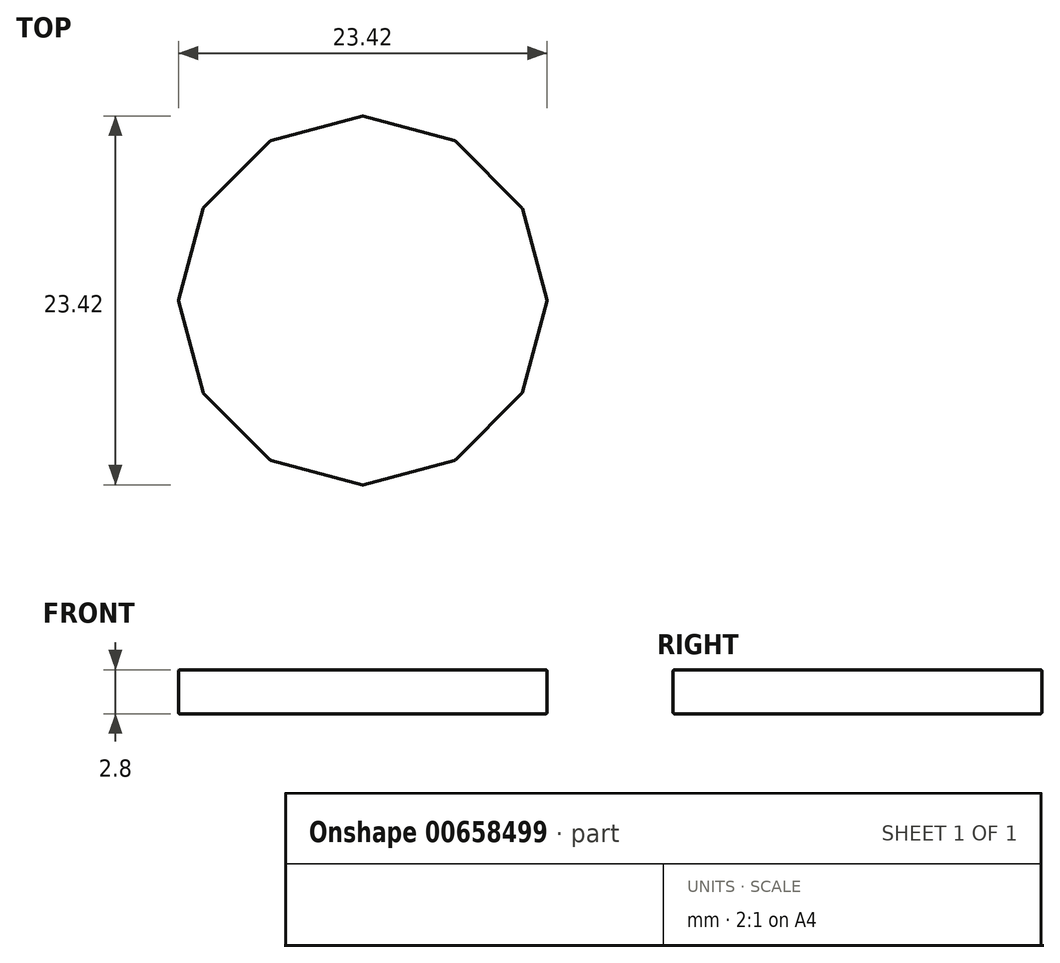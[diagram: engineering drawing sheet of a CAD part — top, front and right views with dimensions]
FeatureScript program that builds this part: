
annotation { "Feature Type Name" : "Feature", "Feature Type Description" : "" }
export const myFeature = defineFeature(function(context is Context, id is Id, definition is map)
    precondition{}
    {
        {
            var Q0;
            Q0=qCreatedBy(makeId("Top.planeOp"),FACE);
            var sketch = newSketch(context, id + "F0", { "sketchPlane" : qUnion([Q0])});
            skCircle(sketch, "E0.cCircle", {"center": v(0, 0) * mm, "radius": 11.71 * mm, "construction": true});
            skLineSegment(sketch, "E0.0", {"start": v(5.86, 10.15) * mm, "end": v(10.15, 5.86) * mm});
            skLineSegment(sketch, "E0.1", {"start": v(10.15, 5.86) * mm, "end": v(11.72, 0) * mm});
            skLineSegment(sketch, "E0.2", {"start": v(11.72, 0) * mm, "end": v(10.15, -5.86) * mm});
            skLineSegment(sketch, "E0.3", {"start": v(10.15, -5.86) * mm, "end": v(5.86, -10.15) * mm});
            skLineSegment(sketch, "E0.4", {"start": v(5.86, -10.15) * mm, "end": v(0, -11.72) * mm});
            skLineSegment(sketch, "E0.5", {"start": v(0, -11.72) * mm, "end": v(-5.86, -10.15) * mm});
            skLineSegment(sketch, "E0.6", {"start": v(-5.86, -10.15) * mm, "end": v(-10.15, -5.86) * mm});
            skLineSegment(sketch, "E0.7", {"start": v(-10.15, -5.86) * mm, "end": v(-11.72, 0) * mm});
            skLineSegment(sketch, "E0.8", {"start": v(-11.72, 0) * mm, "end": v(-10.15, 5.86) * mm});
            skLineSegment(sketch, "E0.9", {"start": v(-10.15, 5.86) * mm, "end": v(-5.86, 10.15) * mm});
            skLineSegment(sketch, "E0.10", {"start": v(-5.86, 10.15) * mm, "end": v(0, 11.72) * mm});
            skLineSegment(sketch, "E0.11", {"start": v(0, 11.72) * mm, "end": v(5.86, 10.15) * mm});
            skSolve(sketch);
        }
        {
            var Q0;
            Q0 = qSketchRegion(id + "F0", true);
            extrude(context, id + "F1", {"entities" : qUnion([Q0]), "depth" : 2.8 * mm, "offsetDistance" : 25 * mm});
        }
        {
            var Q0;
            Q0=makeQuery(id+"F1.opExtrude","CAP_FACE",FACE,{"disambiguationData":[OSD([sQuery(id+"F0.wireOp",EDGE,"E0.0"),sQuery(id+"F0.wireOp",EDGE,"E0.1"),sQuery(id+"F0.wireOp",EDGE,"E0.2"),sQuery(id+"F0.wireOp",EDGE,"E0.3"),sQuery(id+"F0.wireOp",EDGE,"E0.4"),sQuery(id+"F0.wireOp",EDGE,"E0.5"),sQuery(id+"F0.wireOp",EDGE,"E0.6"),sQuery(id+"F0.wireOp",EDGE,"E0.7"),sQuery(id+"F0.wireOp",EDGE,"E0.8"),sQuery(id+"F0.wireOp",EDGE,"E0.9"),sQuery(id+"F0.wireOp",EDGE,"E0.10"),sQuery(id+"F0.wireOp",EDGE,"E0.11")])],"isStart":false});
            var Q1;
            Q1=makeQuery(id+"F1.opExtrude","CAP_FACE",FACE,{"disambiguationData":[OSD([sQuery(id+"F0.wireOp",EDGE,"E0.0"),sQuery(id+"F0.wireOp",EDGE,"E0.1"),sQuery(id+"F0.wireOp",EDGE,"E0.2"),sQuery(id+"F0.wireOp",EDGE,"E0.3"),sQuery(id+"F0.wireOp",EDGE,"E0.4"),sQuery(id+"F0.wireOp",EDGE,"E0.5"),sQuery(id+"F0.wireOp",EDGE,"E0.6"),sQuery(id+"F0.wireOp",EDGE,"E0.7"),sQuery(id+"F0.wireOp",EDGE,"E0.8"),sQuery(id+"F0.wireOp",EDGE,"E0.9"),sQuery(id+"F0.wireOp",EDGE,"E0.10"),sQuery(id+"F0.wireOp",EDGE,"E0.11")])],"isStart":true});
            var Q2;
            Q2=makeQuery(id+"F1.opExtrude","SWEPT_EDGE",EDGE,{"disambiguationData":[OSD([sQuery(id+"F0.wireOp",EDGE,"E0.8"),sQuery(id+"F0.wireOp",EDGE,"E0.9")])]});
            var Q3;
            Q3=makeQuery(id+"F1.opExtrude","SWEPT_EDGE",EDGE,{"disambiguationData":[OSD([sQuery(id+"F0.wireOp",EDGE,"E0.7"),sQuery(id+"F0.wireOp",EDGE,"E0.8")])]});
            var Q4;
            Q4=makeQuery(id+"F1.opExtrude","SWEPT_EDGE",EDGE,{"disambiguationData":[OSD([sQuery(id+"F0.wireOp",EDGE,"E0.6"),sQuery(id+"F0.wireOp",EDGE,"E0.7")])]});
            var Q5;
            Q5=makeQuery(id+"F1.opExtrude","SWEPT_EDGE",EDGE,{"disambiguationData":[OSD([sQuery(id+"F0.wireOp",EDGE,"E0.5"),sQuery(id+"F0.wireOp",EDGE,"E0.6")])]});
            var Q6;
            Q6=makeQuery(id+"F1.opExtrude","SWEPT_EDGE",EDGE,{"disambiguationData":[OSD([sQuery(id+"F0.wireOp",EDGE,"E0.4"),sQuery(id+"F0.wireOp",EDGE,"E0.5")])]});
            var Q7;
            Q7=makeQuery(id+"F1.opExtrude","SWEPT_EDGE",EDGE,{"disambiguationData":[OSD([sQuery(id+"F0.wireOp",EDGE,"E0.3"),sQuery(id+"F0.wireOp",EDGE,"E0.4")])]});
            var Q8;
            Q8=makeQuery(id+"F1.opExtrude","SWEPT_EDGE",EDGE,{"disambiguationData":[OSD([sQuery(id+"F0.wireOp",EDGE,"E0.2"),sQuery(id+"F0.wireOp",EDGE,"E0.3")])]});
            var Q9;
            Q9=makeQuery(id+"F1.opExtrude","SWEPT_EDGE",EDGE,{"disambiguationData":[OSD([sQuery(id+"F0.wireOp",EDGE,"E0.1"),sQuery(id+"F0.wireOp",EDGE,"E0.2")])]});
            var Q10;
            Q10=makeQuery(id+"F1.opExtrude","SWEPT_EDGE",EDGE,{"disambiguationData":[OSD([sQuery(id+"F0.wireOp",EDGE,"E0.0"),sQuery(id+"F0.wireOp",EDGE,"E0.1")])]});
            var Q11;
            Q11=makeQuery(id+"F1.opExtrude","SWEPT_EDGE",EDGE,{"disambiguationData":[OSD([sQuery(id+"F0.wireOp",EDGE,"E0.0"),sQuery(id+"F0.wireOp",EDGE,"E0.11")])]});
            var Q12;
            Q12=makeQuery(id+"F1.opExtrude","SWEPT_EDGE",EDGE,{"disambiguationData":[OSD([sQuery(id+"F0.wireOp",EDGE,"E0.10"),sQuery(id+"F0.wireOp",EDGE,"E0.11")])]});
            var Q13;
            Q13=makeQuery(id+"F1.opExtrude","SWEPT_EDGE",EDGE,{"disambiguationData":[OSD([sQuery(id+"F0.wireOp",EDGE,"E0.9"),sQuery(id+"F0.wireOp",EDGE,"E0.10")])]});
            fillet(context, id + "F2", {"entities" : qUnion([Q0, Q1, Q2, Q3, Q4, Q5, Q6, Q7, Q8, Q9, Q10, Q11, Q12, Q13]), "tangentPropagation" : true, "radius" : 0.1 * mm, "defaultsChanged" : true, "vertexSettings" : [], "allowEdgeOverflow" : false});
        }
    });
